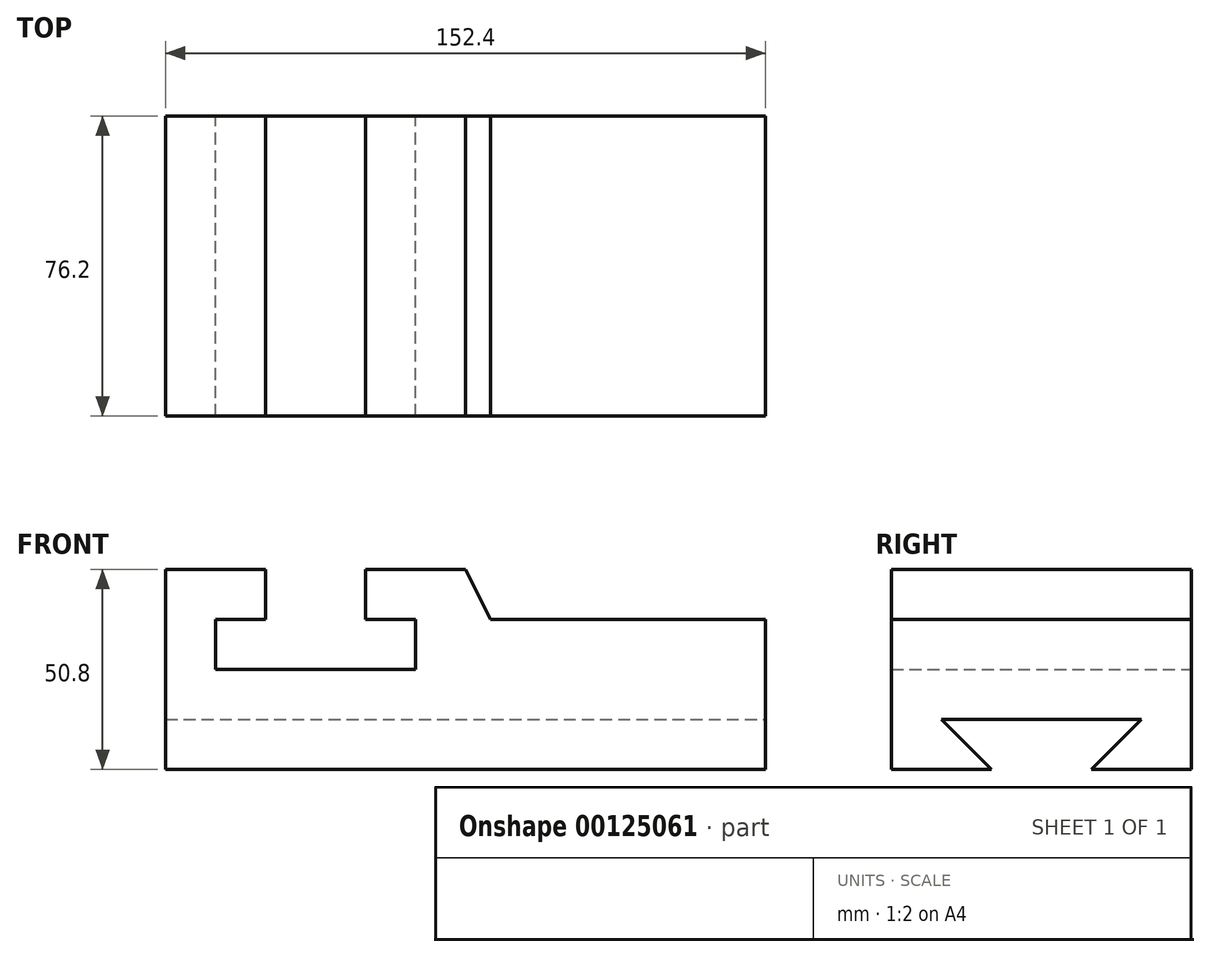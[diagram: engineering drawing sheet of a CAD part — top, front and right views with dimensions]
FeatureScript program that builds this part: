
annotation { "Feature Type Name" : "Feature", "Feature Type Description" : "" }
export const myFeature = defineFeature(function(context is Context, id is Id, definition is map)
    precondition{}
    {
        {
            var Q0;
            Q0=qCreatedBy(makeId("Front.planeOp"),FACE);
            var sketch = newSketch(context, id + "F0", { "sketchPlane" : qUnion([Q0])});
            skLineSegment(sketch, "E0.top", {"start": v(76.2, -25.4) * mm, "end": v(-76.2, -25.4) * mm});
            skLineSegment(sketch, "E0.right", {"start": v(-76.2, 25.4) * mm, "end": v(-76.2, -25.4) * mm});
            skPoint(sketch, "E0.middle", {"position": v(0, 0) * mm});
            skLineSegment(sketch, "E1", {"start": v(-76.2, 25.4) * mm, "end": v(-50.8, 25.4) * mm});
            skLineSegment(sketch, "E2", {"start": v(-50.8, 25.4) * mm, "end": v(-50.8, 12.7) * mm});
            skLineSegment(sketch, "E3", {"start": v(-50.8, 12.7) * mm, "end": v(-63.5, 12.7) * mm});
            skLineSegment(sketch, "E4", {"start": v(-63.5, 12.7) * mm, "end": v(-63.5, 0) * mm});
            skLineSegment(sketch, "E5", {"start": v(-63.5, 0) * mm, "end": v(-12.7, 0) * mm});
            skLineSegment(sketch, "E6", {"start": v(-12.7, 0) * mm, "end": v(-12.7, 12.7) * mm});
            skLineSegment(sketch, "E7", {"start": v(-12.7, 12.7) * mm, "end": v(-25.4, 12.7) * mm});
            skLineSegment(sketch, "E8", {"start": v(-25.4, 12.7) * mm, "end": v(-25.4, 25.4) * mm});
            skLineSegment(sketch, "E9", {"start": v(-25.4, 25.4) * mm, "end": v(0, 25.4) * mm});
            skLineSegment(sketch, "E10", {"start": v(6.35, 12.7) * mm, "end": v(0, 25.4) * mm});
            skLineSegment(sketch, "E11", {"start": v(6.35, 12.7) * mm, "end": v(76.2, 12.7) * mm});
            skLineSegment(sketch, "E12", {"start": v(76.2, 12.7) * mm, "end": v(76.2, -25.4) * mm});
            skSolve(sketch);
        }
        {
            var Q0;
            Q0 = qSketchRegion(id + "F0", true);
            extrude(context, id + "F1", {"entities" : qUnion([Q0]), "endBound" : BoundingType.SYMMETRIC, "depth" : 76.2 * mm});
        }
        {
            var Q0;
            Q0=makeQuery(id+"F1.opExtrude","SWEPT_FACE",FACE,{"disambiguationData":[OSD([sQuery(id+"F0.wireOp",EDGE,"E12")])]});
            var sketch = newSketch(context, id + "F2", { "sketchPlane" : qUnion([Q0])});
            skLineSegment(sketch, "E13", {"start": v(-25.4, -12.7) * mm, "end": v(-12.7, -25.4) * mm});
            skLineSegment(sketch, "E14", {"start": v(25.39, -12.7) * mm, "end": v(12.7, -25.4) * mm});
            skLineSegment(sketch, "E15", {"start": v(-25.4, -12.7) * mm, "end": v(25.39, -12.7) * mm});
            skLineSegment(sketch, "E16", {"start": v(-12.7, -25.4) * mm, "end": v(12.7, -25.4) * mm});
            skSolve(sketch);
        }
        {
            var Q0;
            Q0 = qSketchRegion(id + "F2", true);
            extrude(context, id + "F3", {"entities" : qUnion([Q0]), "operationType" : NewBodyOperationType.REMOVE, "endBound" : BoundingType.THROUGH_ALL, "oppositeDirection" : true, "depth" : 25.4 * mm});
        }
    });
